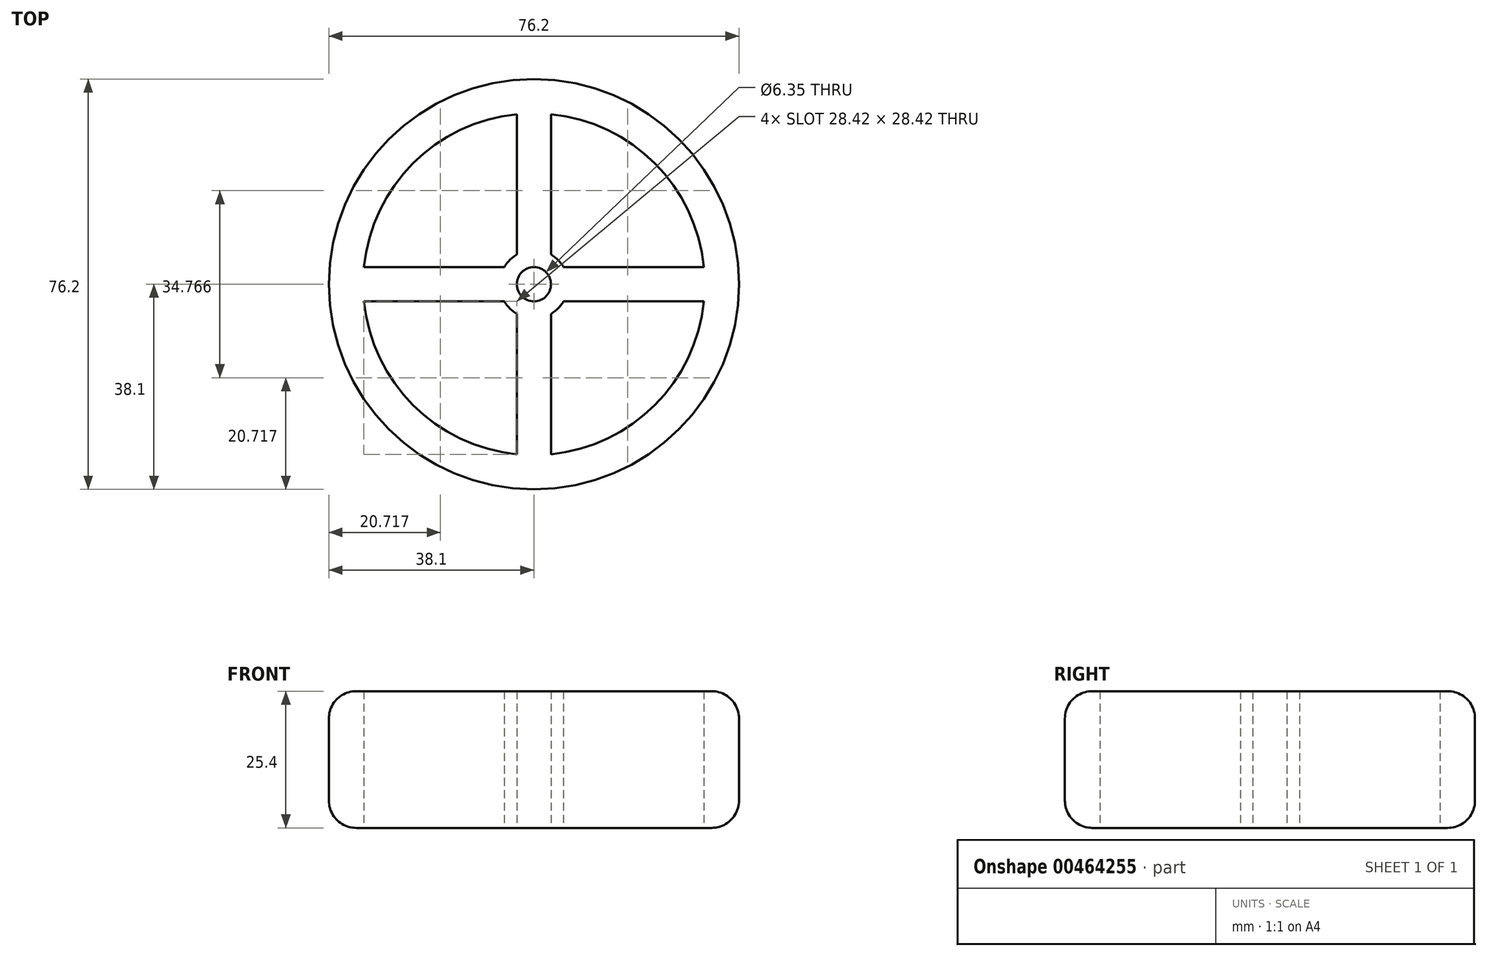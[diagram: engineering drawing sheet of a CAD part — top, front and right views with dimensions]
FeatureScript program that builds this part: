
annotation { "Feature Type Name" : "Feature", "Feature Type Description" : "" }
export const myFeature = defineFeature(function(context is Context, id is Id, definition is map)
    precondition{}
    {
        {
            var Q0;
            Q0=qCreatedBy(makeId("Top.planeOp"),FACE);
            var sketch = newSketch(context, id + "F0", { "sketchPlane" : qUnion([Q0])});
            skCircle(sketch, "E0", {"center": v(0, 0) * mm, "radius": 38.1 * mm});
            skArc(sketch, "E1", {"start": v(-31.6, -3.17) * mm, "mid": v(0, -31.75) * mm, "end": v(31.6, -3.17) * mm});
            skArc(sketch, "E2", {"start": v(-3.18, 5.5) * mm, "mid": v(-4.5, 4.5) * mm, "end": v(-5.5, 3.17) * mm});
            skArc(sketch, "E3", {"start": v(5.5, -3.18) * mm, "mid": v(4.5, -4.5) * mm, "end": v(3.17, -5.5) * mm});
            skCircle(sketch, "E4", {"center": v(0, 0) * mm, "radius": 3.18 * mm});
            skLineSegment(sketch, "E5", {"start": v(3.18, 5.5) * mm, "end": v(3.18, 31.6) * mm});
            skLineSegment(sketch, "E6", {"start": v(-3.18, -5.5) * mm, "end": v(-3.18, -31.6) * mm});
            skLineSegment(sketch, "E7", {"start": v(5.5, 3.18) * mm, "end": v(31.6, 3.18) * mm});
            skLineSegment(sketch, "E8", {"start": v(5.5, -3.18) * mm, "end": v(31.6, -3.18) * mm});
            skLineSegment(sketch, "E9", {"start": v(-5.5, 3.18) * mm, "end": v(-31.6, 3.18) * mm});
            skLineSegment(sketch, "E10", {"start": v(-5.5, -3.18) * mm, "end": v(-31.6, -3.18) * mm});
            skPoint(sketch, "E11.orphan", {"position": v(3.18, 37.97) * mm});
            skPoint(sketch, "E12.orphan", {"position": v(-3.18, 37.97) * mm});
            skPoint(sketch, "E13.orphan", {"position": v(38.1, 0) * mm});
            skLineSegment(sketch, "E14.trimOffspring", {"start": v(37.97, -3.18) * mm, "end": v(38.1, -3.18) * mm});
            skArc(sketch, "E15.trimOffspring", {"start": v(-3.17, 31.6) * mm, "mid": v(-22.45, 22.45) * mm, "end": v(-31.6, 3.18) * mm});
            skArc(sketch, "E16.trimOffspring", {"start": v(31.6, 3.17) * mm, "mid": v(22.45, 22.45) * mm, "end": v(3.18, 31.6) * mm});
            skArc(sketch, "E17.trimOffspring", {"start": v(-5.5, 3.17) * mm, "mid": v(-4.5, 4.5) * mm, "end": v(-3.18, 5.5) * mm});
            skArc(sketch, "E18.trimOffspring", {"start": v(3.18, 5.5) * mm, "mid": v(4.5, 4.5) * mm, "end": v(5.5, 3.18) * mm});
            skPoint(sketch, "E19.orphan", {"position": v(0, 3.18) * mm});
            skLineSegment(sketch, "E20.trimOffspring", {"start": v(-3.18, 5.5) * mm, "end": v(-3.18, 31.6) * mm});
            skArc(sketch, "E21.trimOffspring", {"start": v(-5.5, -3.18) * mm, "mid": v(-4.5, -4.5) * mm, "end": v(-3.18, -5.5) * mm});
            skArc(sketch, "E22.trimOffspring", {"start": v(3.18, -5.5) * mm, "mid": v(4.5, -4.5) * mm, "end": v(5.5, -3.18) * mm});
            skArc(sketch, "E23.trimOffspring", {"start": v(-3.18, -5.5) * mm, "mid": v(-4.5, -4.5) * mm, "end": v(-5.5, -3.17) * mm});
            skLineSegment(sketch, "E24.trimOffspring", {"start": v(3.18, -5.5) * mm, "end": v(3.18, -31.6) * mm});
            skArc(sketch, "E25.trimOffspring", {"start": v(5.5, 3.18) * mm, "mid": v(4.5, 4.5) * mm, "end": v(3.18, 5.5) * mm});
            skPoint(sketch, "E26.end.orphan", {"position": v(0, -3.18) * mm});
            skSolve(sketch);
        }
        {
            var Q0;
            Q0=makeQuery(id+"F0.imprint","IMPRINT",FACE,{"disambiguationData":[TD([[makeQuery(id+"F0.imprint","IMPRINT",EDGE,{"derivedFrom":sQuery(id+"F0.wireOp",EDGE,"E0")}),1.0]])]});
            extrude(context, id + "F1", {"entities" : qUnion([Q0]), "depth" : 25.4 * mm});
        }
        {
            var Q0;
            Q0=makeQuery(id+"F1.opExtrude","CAP_EDGE",EDGE,{"disambiguationData":[OSD([sQuery(id+"F0.wireOp",EDGE,"E0")])],"isStart":false});
            var Q1;
            Q1=makeQuery(id+"F1.opExtrude","CAP_EDGE",EDGE,{"disambiguationData":[OSD([sQuery(id+"F0.wireOp",EDGE,"E0")])],"isStart":true});
            fillet(context, id + "F2", {"entities" : qUnion([Q0, Q1]), "radius" : 5.08 * mm, "tangentPropagation" : true, "allowEdgeOverflow" : false});
        }
    });
